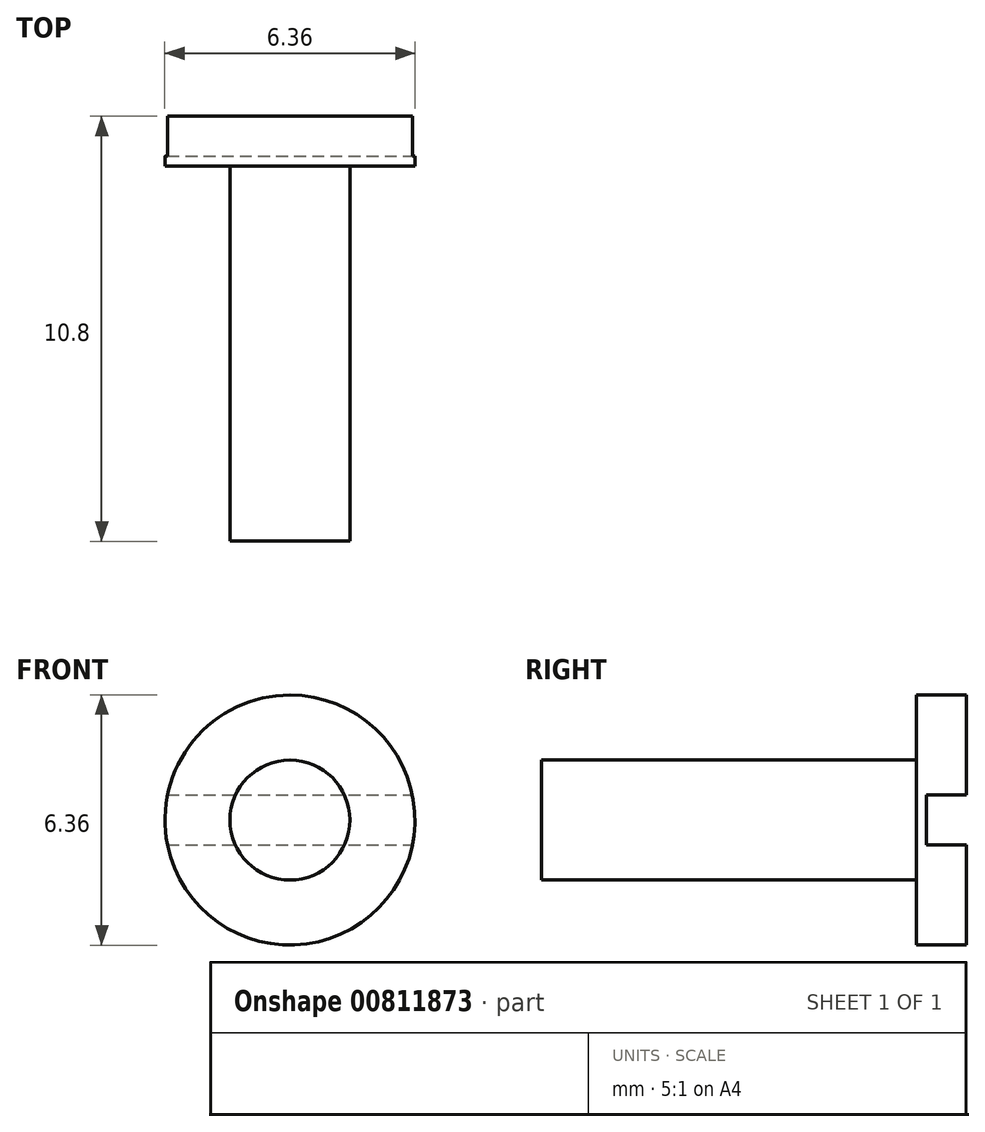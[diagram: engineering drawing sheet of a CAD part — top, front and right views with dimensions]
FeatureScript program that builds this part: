
annotation { "Feature Type Name" : "Feature", "Feature Type Description" : "" }
export const myFeature = defineFeature(function(context is Context, id is Id, definition is map)
    precondition{}
    {
        {
            var Q0;
            Q0=qCreatedBy(makeId("Front.planeOp"),FACE);
            var sketch = newSketch(context, id + "F0", { "sketchPlane" : qUnion([Q0])});
            skCircle(sketch, "E0", {"center": v(0, 0) * mm, "radius": 1.52 * mm});
            skSolve(sketch);
        }
        {
            var Q0;
            Q0=makeQuery(id+"F0.imprint","IMPRINT",FACE,{"disambiguationData":[TD([[makeQuery(id+"F0.imprint","IMPRINT",EDGE,{"derivedFrom":sQuery(id+"F0.wireOp",EDGE,"E0")}),1.0]])]});
            extrude(context, id + "F1", {"entities" : qUnion([Q0]), "depth" : 9.52 * mm, "offsetDistance" : 25.4 * mm});
        }
        {
            var Q0;
            Q0=makeQuery(id+"F1.opExtrude","CAP_FACE",FACE,{"disambiguationData":[OSD([sQuery(id+"F0.wireOp",EDGE,"E0")])],"isStart":true});
            var sketch = newSketch(context, id + "F2", { "sketchPlane" : qUnion([Q0])});
            skCircle(sketch, "E1", {"center": v(0, 0) * mm, "radius": 3.18 * mm});
            skSolve(sketch);
        }
        {
            var Q0;
            Q0 = qSketchRegion(id + "F2", true);
            extrude(context, id + "F3", {"entities" : qUnion([Q0]), "operationType" : NewBodyOperationType.ADD, "depth" : 1.27 * mm, "offsetDistance" : 25.4 * mm});
        }
        {
            var Q0;
            Q0=makeQuery(id+"F3.opExtrude","CAP_FACE",FACE,{"disambiguationData":[OSD([sQuery(id+"F2.wireOp",EDGE,"E1")])],"isStart":false});
            var sketch = newSketch(context, id + "F4", { "sketchPlane" : qUnion([Q0])});
            skLineSegment(sketch, "E2.bottom", {"start": v(3.18, 0.64) * mm, "end": v(-3.18, 0.64) * mm});
            skLineSegment(sketch, "E2.top", {"start": v(3.18, -0.64) * mm, "end": v(-3.18, -0.64) * mm});
            skLineSegment(sketch, "E2.left", {"start": v(3.18, 0.64) * mm, "end": v(3.18, -0.64) * mm});
            skLineSegment(sketch, "E2.right", {"start": v(-3.18, 0.64) * mm, "end": v(-3.18, -0.64) * mm});
            skPoint(sketch, "E2.middle", {"position": v(0, 0) * mm});
            skSolve(sketch);
        }
        {
            var Q0;
            {var subQ0=sQuery(id+"F4.wireOp",EDGE,"E2.bottom");var subQ1=makeQuery(id+"F3.opExtrude","CAP_EDGE",EDGE,{"disambiguationData":[OSD([sQuery(id+"F2.wireOp",EDGE,"E1")])],"isStart":false});var subQ4=makeQuery(id+"F4.imprint","INTERSECT",VERTEX,{"disambiguationData":[OD(0.0)],"derivedFrom":[subQ1,subQ0]});Q0=makeQuery(id+"F4.imprint","IMPRINT",FACE,{"disambiguationData":[TD([[makeQuery(id+"F4.imprint","IMPRINT",EDGE,{"disambiguationData":[TD([[subQ4,-1.0]])],"derivedFrom":subQ0}),1.0]])]});}
            extrude(context, id + "F5", {"entities" : qUnion([Q0]), "operationType" : NewBodyOperationType.REMOVE, "oppositeDirection" : true, "depth" : 1.02 * mm, "offsetDistance" : 25.4 * mm});
        }
    });
